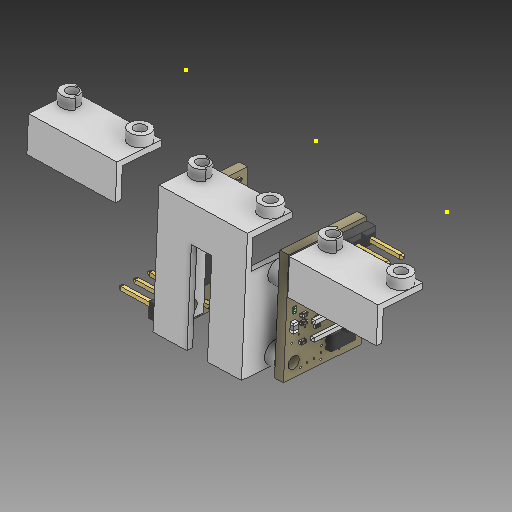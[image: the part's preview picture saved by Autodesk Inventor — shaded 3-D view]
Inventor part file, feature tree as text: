
AUTODESK INVENTOR PART (.ipt)
format: ipt  version: 2020 (Build 240168000, 168)  size: 8,795,648 bytes
history: native  units: mm
features: other x8, sketch x5
ambient origin geometry x8: Origin, YZ Plane, XZ Plane, XY Plane, X Axis, Y Axis, Z Axis, Center Point
bodies: Solid1 (feature_tree)
feature tree (13):
  other  "5DržačaLidara.iam"
  other  "DržačSenzoraUdaljenostiOnlyOne(1)_v.1.0.ipt:1"
  other  "DržačSenzoraUdaljenostiOnlyOne(1)_v.1.0.ipt:2"
  other  "DržačSenzoraUdaljenostiOnlyOne(1)_v.1.0.ipt:3"
  other  "DržačSenzoraUdaljenostiOnlyOne(1)_v.1.0.ipt:4"
  other  "DržačSenzoraUdaljenostiOnlyOne(1)_v.1.0.ipt:5"
  other  "mrm-lid-an.ipt:1"
  other  "mrm-lid-an.ipt:2"
  sketch  "Sketch8"
  sketch  "Sketch8_1"  dims[d0=10.0mm]
  sketch  "Sketch8_2"
  sketch  "Sketch8_3"
  sketch  "Sketch8_4"
